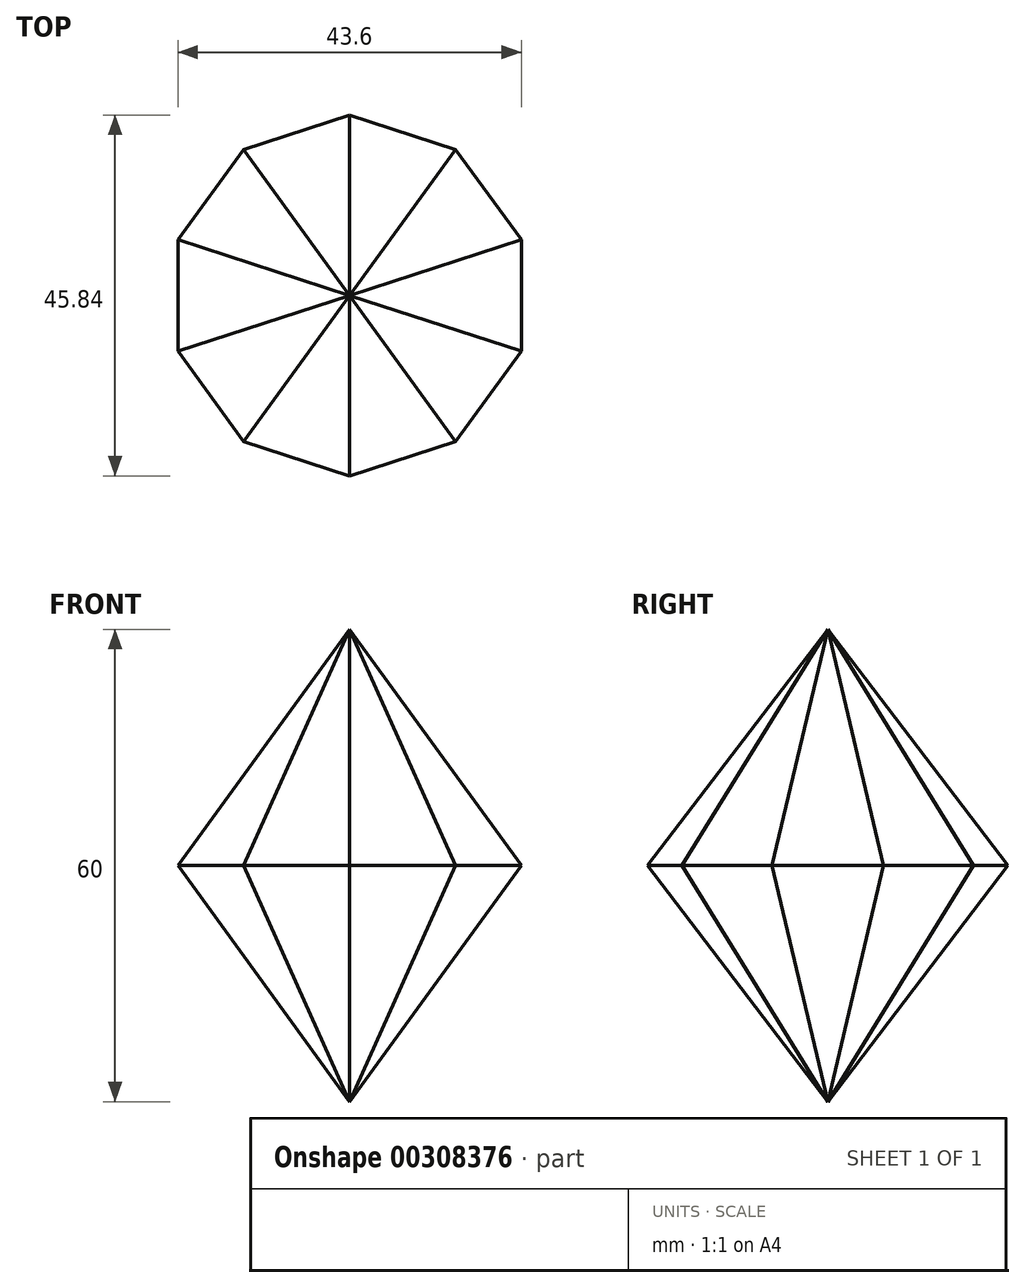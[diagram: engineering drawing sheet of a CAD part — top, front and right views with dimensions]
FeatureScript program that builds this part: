
annotation { "Feature Type Name" : "Feature", "Feature Type Description" : "" }
export const myFeature = defineFeature(function(context is Context, id is Id, definition is map)
    precondition{}
    {
        {
            var Q0;
            Q0=qCreatedBy(makeId("Top.planeOp"),FACE);
            var sketch = newSketch(context, id + "F0", { "sketchPlane" : qUnion([Q0])});
            skCircle(sketch, "E0.cCircle", {"center": v(0, 0) * mm, "radius": 30 * mm, "construction": true});
            skLineSegment(sketch, "E0.0", {"start": v(-21.8, 30) * mm, "end": v(21.8, 30) * mm});
            skLineSegment(sketch, "E0.1", {"start": v(21.8, 30) * mm, "end": v(35.27, -11.46) * mm});
            skLineSegment(sketch, "E0.2", {"start": v(35.27, -11.46) * mm, "end": v(0, -37.08) * mm});
            skLineSegment(sketch, "E0.3", {"start": v(0, -37.08) * mm, "end": v(-35.27, -11.46) * mm});
            skLineSegment(sketch, "E0.4", {"start": v(-35.27, -11.46) * mm, "end": v(-21.8, 30) * mm});
            skPoint(sketch, "E0.0.midPoint", {"position": v(0, 30) * mm});
            skSolve(sketch);
        }
        {
            var Q0;
            Q0 = qSketchRegion(id + "F0", true);
            extrude(context, id + "F1", {"entities" : qUnion([Q0]), "endBound" : BoundingType.SYMMETRIC, "depth" : 60 * mm});
        }
        {
            var Q0;
            Q0=makeQuery(id+"F1.opExtrude","SWEPT_FACE",FACE,{"disambiguationData":[OSD([sQuery(id+"F0.wireOp",EDGE,"E0.3")])]});
            var sketch = newSketch(context, id + "F2", { "sketchPlane" : qUnion([Q0])});
            skLineSegment(sketch, "E1", {"start": v(0, 30) * mm, "end": v(-21.8, 0) * mm});
            skLineSegment(sketch, "E2", {"start": v(-21.8, 0) * mm, "end": v(0, -30) * mm});
            skLineSegment(sketch, "E3", {"start": v(0, -30) * mm, "end": v(21.8, 0) * mm});
            skLineSegment(sketch, "E4", {"start": v(21.8, 0) * mm, "end": v(0, 30) * mm});
            skSolve(sketch);
        }
        {
            var Q0;
            Q0=makeQuery(id+"F1.opExtrude","SWEPT_FACE",FACE,{"disambiguationData":[OSD([sQuery(id+"F0.wireOp",EDGE,"E0.2")])]});
            var sketch = newSketch(context, id + "F3", { "sketchPlane" : qUnion([Q0])});
            skLineSegment(sketch, "E5", {"start": v(-21.8, 0) * mm, "end": v(0, 30) * mm});
            skLineSegment(sketch, "E6", {"start": v(0, 30) * mm, "end": v(21.8, 0) * mm});
            skLineSegment(sketch, "E7", {"start": v(21.8, 0) * mm, "end": v(0, -30) * mm});
            skLineSegment(sketch, "E8", {"start": v(0, -30) * mm, "end": v(-21.8, 0) * mm});
            skSolve(sketch);
        }
        {
            var Q0;
            Q0=makeQuery(id+"F1.opExtrude","SWEPT_FACE",FACE,{"disambiguationData":[OSD([sQuery(id+"F0.wireOp",EDGE,"E0.4")])]});
            var sketch = newSketch(context, id + "F4", { "sketchPlane" : qUnion([Q0])});
            skLineSegment(sketch, "E9", {"start": v(21.8, 0) * mm, "end": v(0, 30) * mm});
            skLineSegment(sketch, "E10", {"start": v(0, 30) * mm, "end": v(-21.8, 0) * mm});
            skLineSegment(sketch, "E11", {"start": v(-21.8, 0) * mm, "end": v(0, -30) * mm});
            skLineSegment(sketch, "E12", {"start": v(0, -30) * mm, "end": v(21.8, 0) * mm});
            skSolve(sketch);
        }
        {
            var Q0;
            Q0=makeQuery(id+"F1.opExtrude","SWEPT_FACE",FACE,{"disambiguationData":[OSD([sQuery(id+"F0.wireOp",EDGE,"E0.1")])]});
            var sketch = newSketch(context, id + "F5", { "sketchPlane" : qUnion([Q0])});
            skLineSegment(sketch, "E13", {"start": v(21.8, 0) * mm, "end": v(0, 30) * mm});
            skLineSegment(sketch, "E14", {"start": v(0, 30) * mm, "end": v(-21.8, 0) * mm});
            skLineSegment(sketch, "E15", {"start": v(-21.8, 0) * mm, "end": v(0, -30) * mm});
            skLineSegment(sketch, "E16", {"start": v(0, -30) * mm, "end": v(21.8, 0) * mm});
            skSolve(sketch);
        }
        {
            var Q0;
            Q0=makeQuery(id+"F1.opExtrude","SWEPT_FACE",FACE,{"disambiguationData":[OSD([sQuery(id+"F0.wireOp",EDGE,"E0.0")])]});
            var sketch = newSketch(context, id + "F6", { "sketchPlane" : qUnion([Q0])});
            skLineSegment(sketch, "E17", {"start": v(21.8, 0) * mm, "end": v(0, 30) * mm});
            skLineSegment(sketch, "E18", {"start": v(0, 30) * mm, "end": v(-21.8, 0) * mm});
            skLineSegment(sketch, "E19", {"start": v(-21.8, 0) * mm, "end": v(0, -30) * mm});
            skLineSegment(sketch, "E20", {"start": v(0, -30) * mm, "end": v(21.8, 0) * mm});
            skSolve(sketch);
        }
        {
            var Q0;
            Q0 = qSketchRegion(id + "F2", true);
            extrude(context, id + "F7", {"entities" : qUnion([Q0]), "operationType" : NewBodyOperationType.INTERSECT, "endBound" : BoundingType.THROUGH_ALL, "oppositeDirection" : true, "depth" : 25 * mm});
        }
        {
            var Q0;
            Q0 = qSketchRegion(id + "F3", true);
            extrude(context, id + "F8", {"entities" : qUnion([Q0]), "operationType" : NewBodyOperationType.INTERSECT, "endBound" : BoundingType.THROUGH_ALL, "oppositeDirection" : true, "depth" : 25 * mm});
        }
        {
            var Q0;
            Q0 = qSketchRegion(id + "F4", true);
            extrude(context, id + "F9", {"entities" : qUnion([Q0]), "operationType" : NewBodyOperationType.INTERSECT, "endBound" : BoundingType.THROUGH_ALL, "oppositeDirection" : true, "depth" : 25 * mm});
        }
        {
            var Q0;
            Q0 = qSketchRegion(id + "F5", true);
            extrude(context, id + "F10", {"entities" : qUnion([Q0]), "operationType" : NewBodyOperationType.INTERSECT, "endBound" : BoundingType.THROUGH_ALL, "oppositeDirection" : true, "depth" : 25 * mm});
        }
        {
            var Q0;
            Q0 = qSketchRegion(id + "F6", true);
            extrude(context, id + "F11", {"entities" : qUnion([Q0]), "operationType" : NewBodyOperationType.INTERSECT, "endBound" : BoundingType.THROUGH_ALL, "oppositeDirection" : true, "depth" : 25 * mm});
        }
    });
